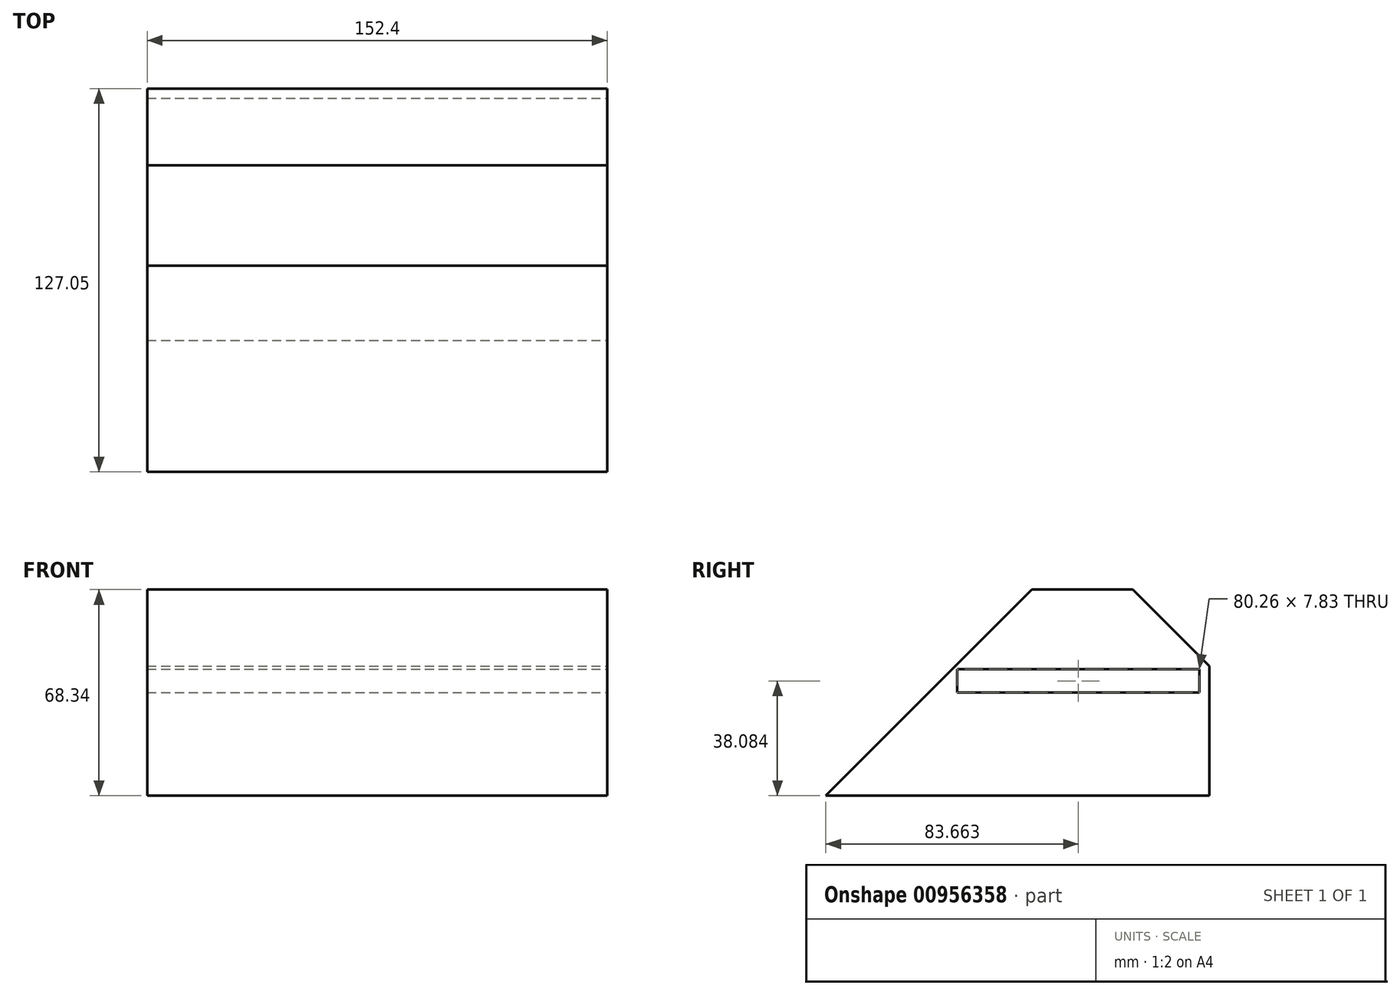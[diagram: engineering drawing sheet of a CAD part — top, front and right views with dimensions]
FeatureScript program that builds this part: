
annotation { "Feature Type Name" : "Feature", "Feature Type Description" : "" }
export const myFeature = defineFeature(function(context is Context, id is Id, definition is map)
    precondition{}
    {
        {
            var Q0;
            Q0=qCreatedBy(makeId("Right.planeOp"),FACE);
            var sketch = newSketch(context, id + "F0", { "sketchPlane" : qUnion([Q0])});
            skLineSegment(sketch, "E0.bottom", {"start": v(67.46, 34.17) * mm, "end": v(-67.46, 34.17) * mm});
            skLineSegment(sketch, "E0.top", {"start": v(67.46, -34.17) * mm, "end": v(-67.46, -34.17) * mm});
            skLineSegment(sketch, "E0.left", {"start": v(67.46, 34.17) * mm, "end": v(67.46, -34.17) * mm});
            skLineSegment(sketch, "E0.right", {"start": v(-67.46, 34.17) * mm, "end": v(-67.46, -34.17) * mm});
            skPoint(sketch, "E0.middle", {"position": v(0, 0) * mm});
            skSolve(sketch);
        }
        {
            var Q0;
            Q0=makeQuery(id+"F0.imprint","IMPRINT",FACE,{"disambiguationData":[TD([[makeQuery(id+"F0.imprint","IMPRINT",EDGE,{"derivedFrom":sQuery(id+"F0.wireOp",EDGE,"E0.bottom")}),1.0]])]});
            extrude(context, id + "F1", {"entities" : qUnion([Q0]), "depth" : 76.2 * mm, "offsetDistance" : 25.4 * mm, "hasSecondDirection" : true, "secondDirectionOppositeDirection" : true, "secondDirectionDepth" : 76.2 * mm});
        }
        {
            var Q0;
            Q0=makeQuery(id+"F1.opExtrude","SWEPT_EDGE",EDGE,{"disambiguationData":[OSD([sQuery(id+"F0.wireOp",EDGE,"E0.bottom"),sQuery(id+"F0.wireOp",EDGE,"E0.right")])]});
            chamfer(context, id + "F2", {"entities" : qUnion([Q0]), "width" : 76.2 * mm, "tangentPropagation" : true});
        }
        {
            var Q0;
            Q0=makeQuery(id+"F1.opExtrude","SWEPT_EDGE",EDGE,{"disambiguationData":[OSD([sQuery(id+"F0.wireOp",EDGE,"E0.bottom"),sQuery(id+"F0.wireOp",EDGE,"E0.left")])]});
            chamfer(context, id + "F3", {"entities" : qUnion([Q0]), "width" : 25.4 * mm, "tangentPropagation" : true});
        }
        {
            var Q0;
            Q0=qCreatedBy(makeId("Right.planeOp"),FACE);
            var sketch = newSketch(context, id + "F4", { "sketchPlane" : qUnion([Q0])});
            skLineSegment(sketch, "E1.bottom", {"start": v(-16.06, 0) * mm, "end": v(64.2, 0) * mm});
            skLineSegment(sketch, "E1.top", {"start": v(-16.06, 7.83) * mm, "end": v(64.2, 7.83) * mm});
            skLineSegment(sketch, "E1.left", {"start": v(-16.06, 0) * mm, "end": v(-16.06, 7.83) * mm});
            skLineSegment(sketch, "E1.right", {"start": v(64.2, 0) * mm, "end": v(64.2, 7.83) * mm});
            skSolve(sketch);
        }
        {
            var Q0;
            Q0 = qSketchRegion(id + "F4", true);
            extrude(context, id + "F5", {"entities" : qUnion([Q0]), "operationType" : NewBodyOperationType.REMOVE, "oppositeDirection" : true, "depth" : 76.2 * mm, "offsetDistance" : 25.4 * mm, "hasSecondDirection" : true, "secondDirectionOppositeDirection" : false, "secondDirectionDepth" : 76.2 * mm});
        }
    });
